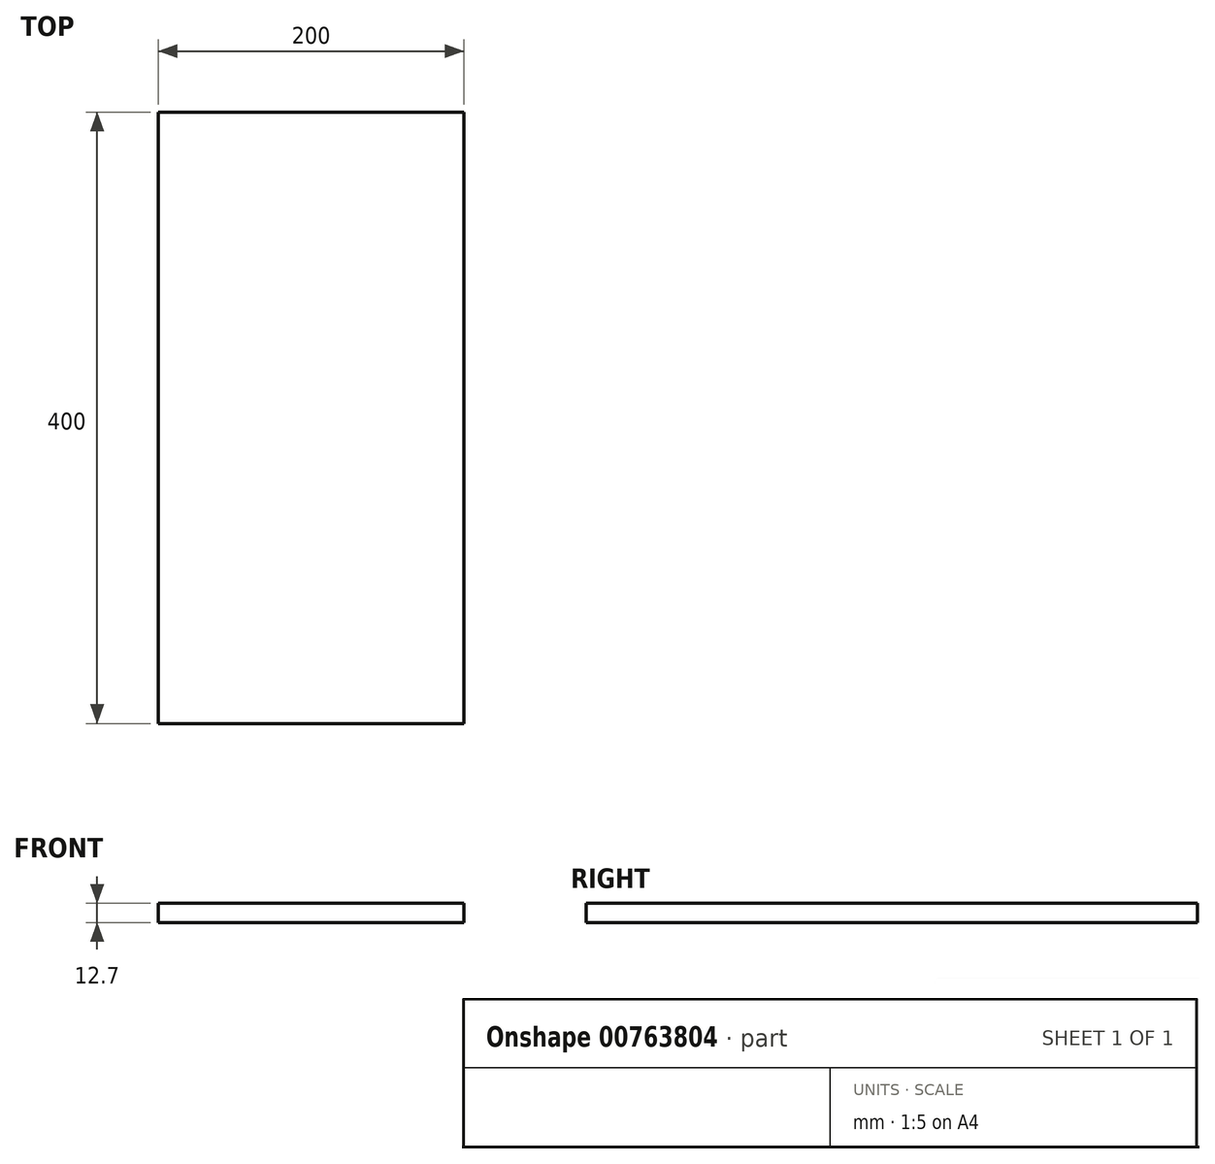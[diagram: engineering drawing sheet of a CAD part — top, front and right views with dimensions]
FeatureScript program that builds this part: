
annotation { "Feature Type Name" : "Feature", "Feature Type Description" : "" }
export const myFeature = defineFeature(function(context is Context, id is Id, definition is map)
    precondition{}
    {
        {
            var Q0;
            Q0=qCreatedBy(makeId("Top.planeOp"),FACE);
            var sketch = newSketch(context, id + "F0", { "sketchPlane" : qUnion([Q0])});
            skLineSegment(sketch, "E0.bottom", {"start": v(100, 200) * mm, "end": v(-100, 200) * mm});
            skLineSegment(sketch, "E0.top", {"start": v(100, -200) * mm, "end": v(-100, -200) * mm});
            skLineSegment(sketch, "E0.left", {"start": v(100, 200) * mm, "end": v(100, -200) * mm});
            skLineSegment(sketch, "E0.right", {"start": v(-100, 200) * mm, "end": v(-100, -200) * mm});
            skPoint(sketch, "E0.middle", {"position": v(0, 0) * mm});
            skSolve(sketch);
        }
        {
            var Q0;
            Q0 = qSketchRegion(id + "F0", true);
            extrude(context, id + "F1", {"entities" : qUnion([Q0]), "depth" : (25.4 / 2) * mm, "offsetDistance" : 25 * mm});
        }
    });
